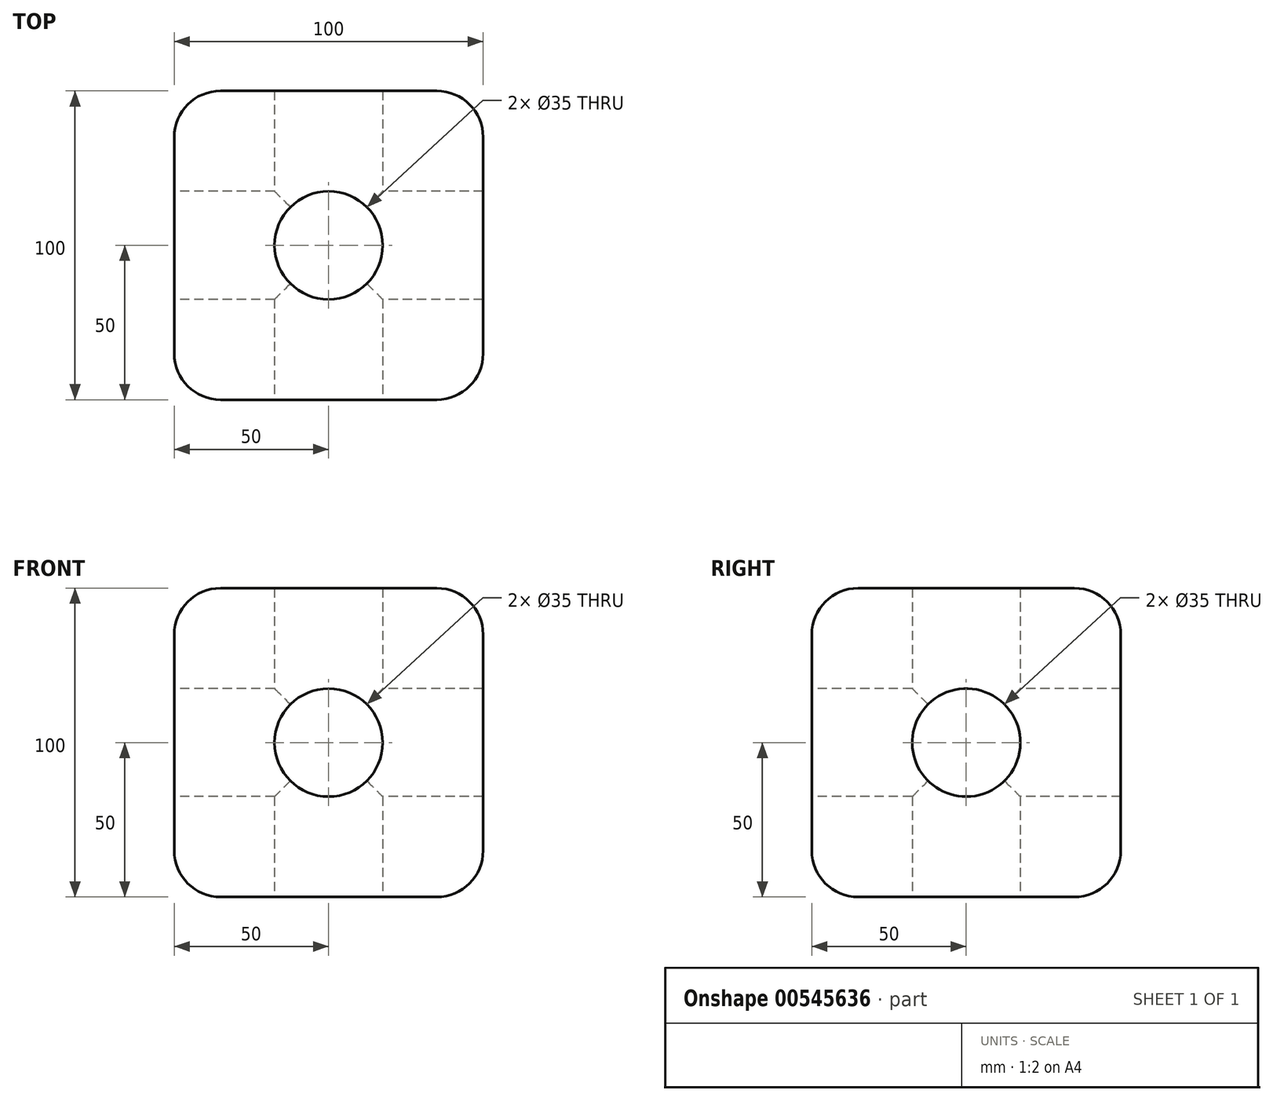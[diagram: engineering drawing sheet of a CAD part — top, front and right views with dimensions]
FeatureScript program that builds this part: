
annotation { "Feature Type Name" : "Feature", "Feature Type Description" : "" }
export const myFeature = defineFeature(function(context is Context, id is Id, definition is map)
    precondition{}
    {
        {
            var Q0;
            Q0=qCreatedBy(makeId("Front.planeOp"),FACE);
            var sketch = newSketch(context, id + "F0", { "sketchPlane" : qUnion([Q0])});
            skLineSegment(sketch, "E0.bottom", {"start": v(50, 50) * mm, "end": v(-50, 50) * mm});
            skLineSegment(sketch, "E0.top", {"start": v(50, -50) * mm, "end": v(-50, -50) * mm});
            skLineSegment(sketch, "E0.left", {"start": v(50, 50) * mm, "end": v(50, -50) * mm});
            skLineSegment(sketch, "E0.right", {"start": v(-50, 50) * mm, "end": v(-50, -50) * mm});
            skPoint(sketch, "E0.middle", {"position": v(0, 0) * mm});
            skSolve(sketch);
        }
        {
            var Q0;
            Q0=makeQuery(id+"F0.imprint","IMPRINT",FACE,{"disambiguationData":[TD([[makeQuery(id+"F0.imprint","IMPRINT",EDGE,{"derivedFrom":sQuery(id+"F0.wireOp",EDGE,"E0.bottom")}),1.0]])]});
            extrude(context, id + "F1", {"entities" : qUnion([Q0]), "endBound" : BoundingType.SYMMETRIC, "depth" : 100 * mm, "offsetDistance" : 25 * mm});
        }
        {
            var Q0;
            Q0=makeQuery(id+"F1.opExtrude","SWEPT_FACE",FACE,{"disambiguationData":[OSD([sQuery(id+"F0.wireOp",EDGE,"E0.right")])]});
            var sketch = newSketch(context, id + "F2", { "sketchPlane" : qUnion([Q0])});
            skCircle(sketch, "E1", {"center": v(0, 0) * mm, "radius": 17.5 * mm});
            skSolve(sketch);
        }
        {
            var Q0;
            Q0=makeQuery(id+"F2.imprint","IMPRINT",FACE,{"disambiguationData":[TD([[makeQuery(id+"F2.imprint","IMPRINT",EDGE,{"derivedFrom":sQuery(id+"F2.wireOp",EDGE,"E1")}),1.0]])]});
            extrude(context, id + "F3", {"entities" : qUnion([Q0]), "operationType" : NewBodyOperationType.ADD, "endBound" : BoundingType.UP_TO_NEXT, "oppositeDirection" : true, "depth" : 25 * mm, "offsetDistance" : 25 * mm});
        }
        {
            var Q0;
            Q0=makeQuery(id+"F2.imprint","IMPRINT",FACE,{"disambiguationData":[TD([[makeQuery(id+"F2.imprint","IMPRINT",EDGE,{"derivedFrom":sQuery(id+"F2.wireOp",EDGE,"E1")}),1.0]])]});
            extrude(context, id + "F4", {"entities" : qUnion([Q0]), "operationType" : NewBodyOperationType.REMOVE, "endBound" : BoundingType.UP_TO_NEXT, "oppositeDirection" : true, "depth" : 25 * mm, "offsetDistance" : 25 * mm});
        }
        {
            var Q0;
            Q0=makeQuery(id+"F1.opExtrude","CAP_FACE",FACE,{"disambiguationData":[OSD([sQuery(id+"F0.wireOp",EDGE,"E0.bottom"),sQuery(id+"F0.wireOp",EDGE,"E0.top"),sQuery(id+"F0.wireOp",EDGE,"E0.left"),sQuery(id+"F0.wireOp",EDGE,"E0.right")])],"isStart":false});
            var sketch = newSketch(context, id + "F5", { "sketchPlane" : qUnion([Q0])});
            skCircle(sketch, "E2", {"center": v(0, 0) * mm, "radius": 17.5 * mm});
            skSolve(sketch);
        }
        {
            var Q0;
            Q0=makeQuery(id+"F5.imprint","IMPRINT",FACE,{"disambiguationData":[TD([[makeQuery(id+"F5.imprint","IMPRINT",EDGE,{"derivedFrom":sQuery(id+"F5.wireOp",EDGE,"E2")}),1.0]])]});
            var Q1;
            Q1=makeQuery(id+"F1.opExtrude","CAP_FACE",FACE,{"disambiguationData":[OSD([sQuery(id+"F0.wireOp",EDGE,"E0.bottom"),sQuery(id+"F0.wireOp",EDGE,"E0.top"),sQuery(id+"F0.wireOp",EDGE,"E0.left"),sQuery(id+"F0.wireOp",EDGE,"E0.right")])],"isStart":true});
            extrude(context, id + "F6", {"entities" : qUnion([Q0]), "operationType" : NewBodyOperationType.REMOVE, "endBound" : BoundingType.UP_TO_SURFACE, "oppositeDirection" : true, "depth" : 25 * mm, "endBoundEntityFace" : qUnion([Q1]), "offsetDistance" : 25 * mm});
        }
        {
            var Q0;
            Q0=makeQuery(id+"F1.opExtrude","SWEPT_FACE",FACE,{"disambiguationData":[OSD([sQuery(id+"F0.wireOp",EDGE,"E0.top")])]});
            var sketch = newSketch(context, id + "F7", { "sketchPlane" : qUnion([Q0])});
            skCircle(sketch, "E3", {"center": v(0, 0) * mm, "radius": 17.5 * mm});
            skSolve(sketch);
        }
        {
            var Q0;
            Q0=makeQuery(id+"F7.imprint","IMPRINT",FACE,{"disambiguationData":[TD([[makeQuery(id+"F7.imprint","IMPRINT",EDGE,{"derivedFrom":sQuery(id+"F7.wireOp",EDGE,"E3")}),1.0]])]});
            var Q1;
            Q1=makeQuery(id+"F1.opExtrude","SWEPT_FACE",FACE,{"disambiguationData":[OSD([sQuery(id+"F0.wireOp",EDGE,"E0.bottom")])]});
            extrude(context, id + "F8", {"entities" : qUnion([Q0]), "operationType" : NewBodyOperationType.REMOVE, "endBound" : BoundingType.UP_TO_SURFACE, "oppositeDirection" : true, "depth" : 25 * mm, "endBoundEntityFace" : qUnion([Q1]), "offsetDistance" : 25 * mm});
        }
        {
            var Q0;
            Q0=makeQuery(id+"F1.opExtrude","CAP_EDGE",EDGE,{"disambiguationData":[OSD([sQuery(id+"F0.wireOp",EDGE,"E0.right")])],"isStart":false});
            var Q1;
            Q1=makeQuery(id+"F1.opExtrude","CAP_EDGE",EDGE,{"disambiguationData":[OSD([sQuery(id+"F0.wireOp",EDGE,"E0.bottom")])],"isStart":false});
            var Q2;
            Q2=makeQuery(id+"F1.opExtrude","CAP_EDGE",EDGE,{"disambiguationData":[OSD([sQuery(id+"F0.wireOp",EDGE,"E0.top")])],"isStart":false});
            var Q3;
            Q3=makeQuery(id+"F1.opExtrude","CAP_EDGE",EDGE,{"disambiguationData":[OSD([sQuery(id+"F0.wireOp",EDGE,"E0.left")])],"isStart":false});
            var Q4;
            Q4=makeQuery(id+"F1.opExtrude","SWEPT_EDGE",EDGE,{"disambiguationData":[OSD([sQuery(id+"F0.wireOp",EDGE,"E0.top"),sQuery(id+"F0.wireOp",EDGE,"E0.left")])]});
            var Q5;
            Q5=makeQuery(id+"F1.opExtrude","SWEPT_EDGE",EDGE,{"disambiguationData":[OSD([sQuery(id+"F0.wireOp",EDGE,"E0.bottom"),sQuery(id+"F0.wireOp",EDGE,"E0.left")])]});
            var Q6;
            Q6=makeQuery(id+"F1.opExtrude","SWEPT_EDGE",EDGE,{"disambiguationData":[OSD([sQuery(id+"F0.wireOp",EDGE,"E0.bottom"),sQuery(id+"F0.wireOp",EDGE,"E0.right")])]});
            var Q7;
            Q7=makeQuery(id+"F1.opExtrude","CAP_EDGE",EDGE,{"disambiguationData":[OSD([sQuery(id+"F0.wireOp",EDGE,"E0.bottom")])],"isStart":true});
            var Q8;
            Q8=makeQuery(id+"F1.opExtrude","CAP_EDGE",EDGE,{"disambiguationData":[OSD([sQuery(id+"F0.wireOp",EDGE,"E0.left")])],"isStart":true});
            var Q9;
            Q9=makeQuery(id+"F1.opExtrude","CAP_EDGE",EDGE,{"disambiguationData":[OSD([sQuery(id+"F0.wireOp",EDGE,"E0.right")])],"isStart":true});
            var Q10;
            Q10=makeQuery(id+"F1.opExtrude","CAP_EDGE",EDGE,{"disambiguationData":[OSD([sQuery(id+"F0.wireOp",EDGE,"E0.top")])],"isStart":true});
            var Q11;
            Q11=makeQuery(id+"F1.opExtrude","SWEPT_EDGE",EDGE,{"disambiguationData":[OSD([sQuery(id+"F0.wireOp",EDGE,"E0.top"),sQuery(id+"F0.wireOp",EDGE,"E0.right")])]});
            fillet(context, id + "F9", {"entities" : qUnion([Q0, Q1, Q2, Q3, Q4, Q5, Q6, Q7, Q8, Q9, Q10, Q11]), "radius" : 15 * mm, "tangentPropagation" : true, "allowEdgeOverflow" : false});
        }
    });
